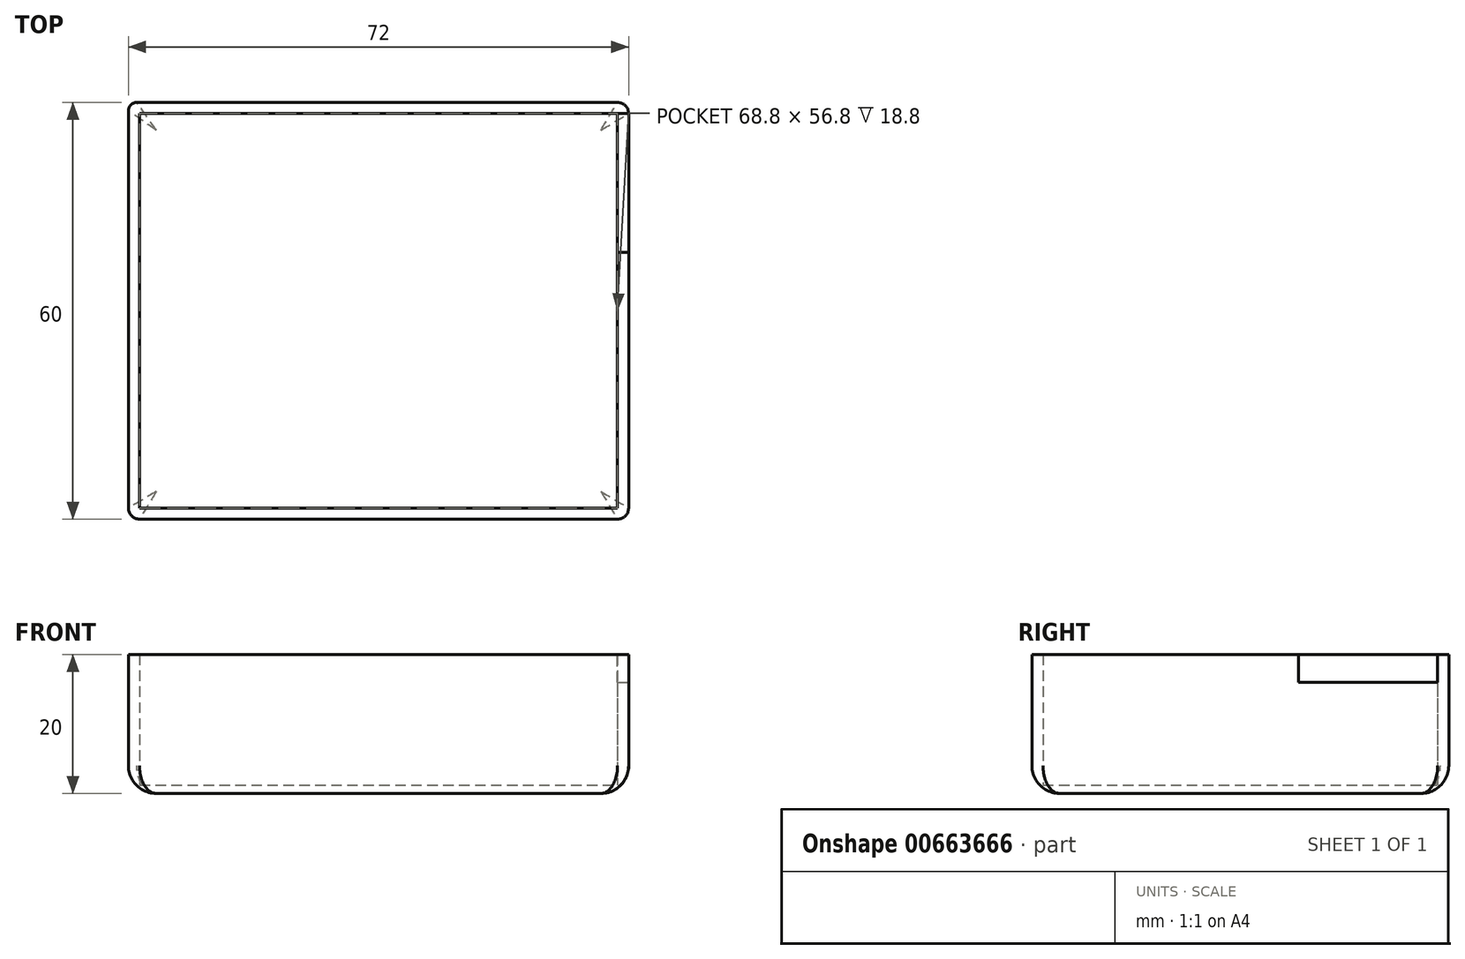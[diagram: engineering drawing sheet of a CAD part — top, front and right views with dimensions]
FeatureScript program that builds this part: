
annotation { "Feature Type Name" : "Feature", "Feature Type Description" : "" }
export const myFeature = defineFeature(function(context is Context, id is Id, definition is map)
    precondition{}
    {
        {
            var Q0;
            Q0=qCreatedBy(makeId("Top.planeOp"),FACE);
            var sketch = newSketch(context, id + "F0", { "sketchPlane" : qUnion([Q0])});
            skLineSegment(sketch, "E0.bottom", {"start": v(1.6, 0) * mm, "end": v(70.4, 0) * mm});
            skLineSegment(sketch, "E0.top", {"start": v(1.2, 60) * mm, "end": v(70.4, 60) * mm});
            skLineSegment(sketch, "E0.left", {"start": v(0, 1.6) * mm, "end": v(0, 58.8) * mm});
            skLineSegment(sketch, "E0.right", {"start": v(72, 1.6) * mm, "end": v(72, 58.4) * mm});
            skLineSegment(sketch, "E1.0", {"start": v(1.6, 58.4) * mm, "end": v(70.4, 58.4) * mm});
            skLineSegment(sketch, "E1.1", {"start": v(1.6, 1.6) * mm, "end": v(1.6, 58.4) * mm});
            skLineSegment(sketch, "E1.2", {"start": v(1.6, 1.6) * mm, "end": v(70.4, 1.6) * mm});
            skLineSegment(sketch, "E1.3", {"start": v(70.4, 1.6) * mm, "end": v(70.4, 58.4) * mm});
            skArc(sketch, "E2", {"start": v(1.2, 60) * mm, "mid": v(0.35, 59.65) * mm, "end": v(0, 58.8) * mm});
            skArc(sketch, "E3", {"start": v(72, 58.4) * mm, "mid": v(71.53, 59.53) * mm, "end": v(70.4, 60) * mm});
            skArc(sketch, "E4", {"start": v(70.4, 0) * mm, "mid": v(71.53, 0.47) * mm, "end": v(72, 1.6) * mm});
            skArc(sketch, "E5", {"start": v(0, 1.6) * mm, "mid": v(0.47, 0.47) * mm, "end": v(1.6, 0) * mm});
            skSolve(sketch);
        }
        {
            var Q0;
            Q0=makeQuery(id+"F0.imprint","IMPRINT",FACE,{"disambiguationData":[TD([[makeQuery(id+"F0.imprint","IMPRINT",EDGE,{"derivedFrom":sQuery(id+"F0.wireOp",EDGE,"E1.0")}),-1.0]])]});
            extrude(context, id + "F1", {"entities" : qUnion([Q0]), "depth" : 1.2 * mm, "offsetDistance" : 25 * mm});
        }
        {
            var Q0;
            Q0 = qSketchRegion(id + "F0", true);
            extrude(context, id + "F2", {"entities" : qUnion([Q0]), "operationType" : NewBodyOperationType.ADD, "depth" : 20 * mm, "offsetDistance" : 25 * mm});
        }
        {
            var Q0;
            Q0=makeQuery(id+"F2.opExtrude","CAP_EDGE",EDGE,{"disambiguationData":[OSD([sQuery(id+"F0.wireOp",EDGE,"E0.bottom")])],"isStart":true});
            fillet(context, id + "F3", {"entities" : qUnion([Q0]), "radius" : 4 * mm, "tangentPropagation" : true, "allowEdgeOverflow" : false});
        }
        {
            var Q0;
            Q0=makeQuery(id+"F2.opExtrude","SWEPT_FACE",FACE,{"disambiguationData":[OSD([sQuery(id+"F0.wireOp",EDGE,"E0.right")])]});
            var sketch = newSketch(context, id + "F4", { "sketchPlane" : qUnion([Q0])});
            skLineSegment(sketch, "E6.bottom", {"start": v(58.4, 20) * mm, "end": v(38.4, 20) * mm});
            skLineSegment(sketch, "E6.top", {"start": v(58.4, 16) * mm, "end": v(38.4, 16) * mm});
            skLineSegment(sketch, "E6.left", {"start": v(58.4, 20) * mm, "end": v(58.4, 16) * mm});
            skLineSegment(sketch, "E6.right", {"start": v(38.4, 20) * mm, "end": v(38.4, 16) * mm});
            skSolve(sketch);
        }
        {
            var Q0;
            Q0=makeQuery(id+"F4.imprint","IMPRINT",FACE,{"disambiguationData":[TD([[makeQuery(id+"F4.imprint","IMPRINT",EDGE,{"derivedFrom":sQuery(id+"F4.wireOp",EDGE,"E6.bottom")}),-1.0]])]});
            extrude(context, id + "F5", {"entities" : qUnion([Q0]), "operationType" : NewBodyOperationType.REMOVE, "oppositeDirection" : true, "depth" : 25 * mm, "offsetDistance" : 25 * mm});
        }
    });
